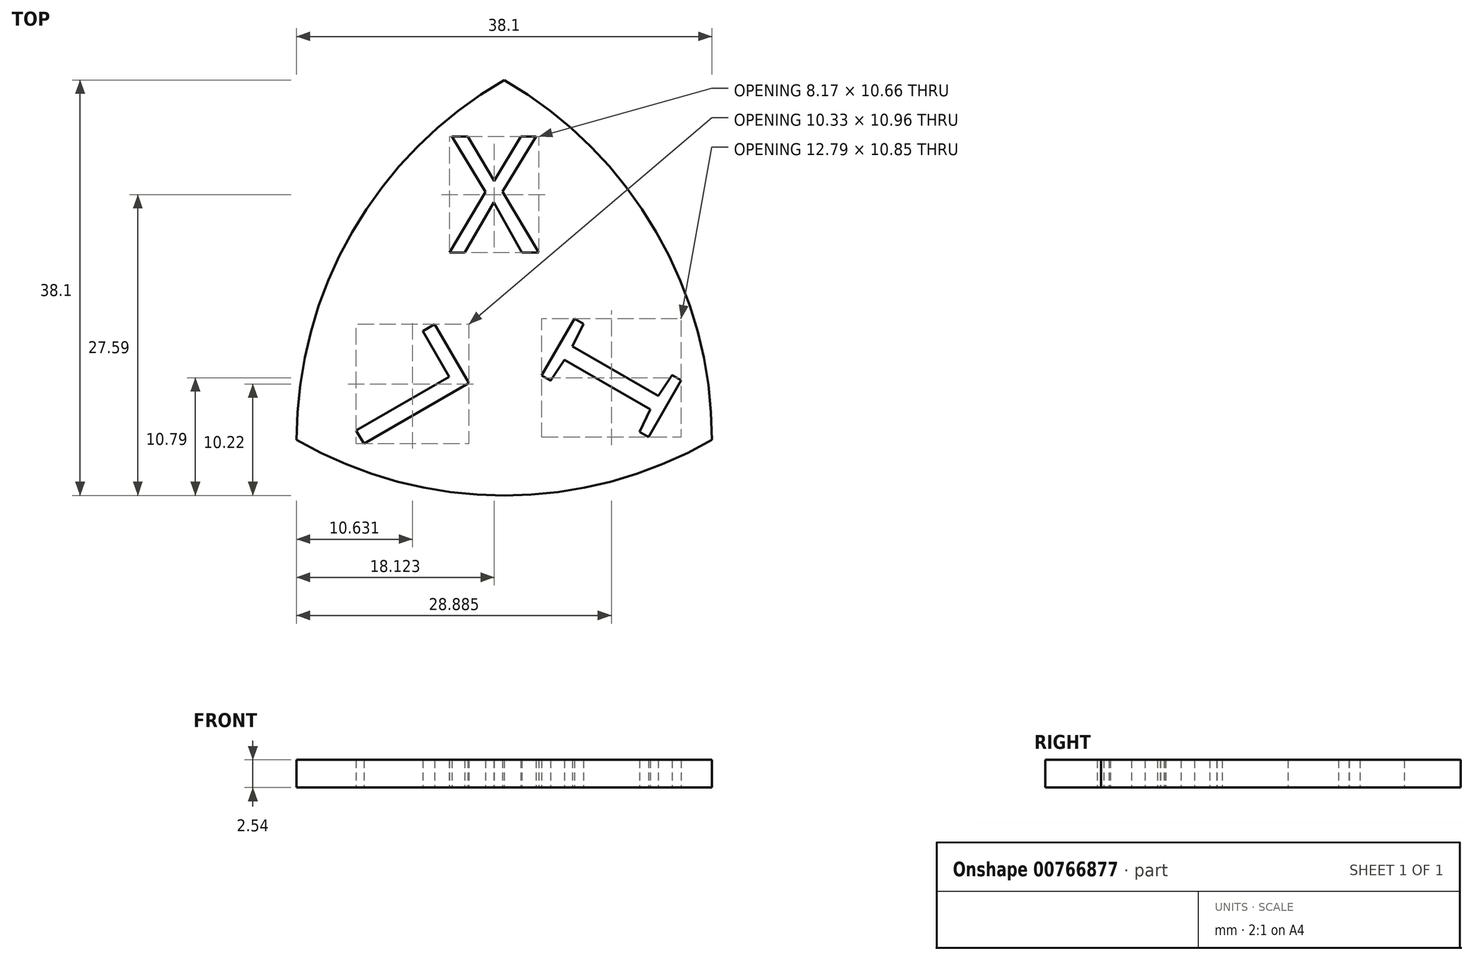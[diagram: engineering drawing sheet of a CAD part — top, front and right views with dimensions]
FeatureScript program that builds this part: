
annotation { "Feature Type Name" : "Feature", "Feature Type Description" : "" }
export const myFeature = defineFeature(function(context is Context, id is Id, definition is map)
    precondition{}
    {
        {
            var Q0;
            Q0=qCreatedBy(makeId("Top.planeOp"),FACE);
            var sketch = newSketch(context, id + "F0", { "sketchPlane" : qUnion([Q0])});
            skCircle(sketch, "E0", {"center": v(0, 0) * mm, "radius": 38.1 * mm});
            skSolve(sketch);
        }
        {
            var Q0;
            Q0=qCreatedBy(makeId("Top.planeOp"),FACE);
            var sketch = newSketch(context, id + "F1", { "sketchPlane" : qUnion([Q0])});
            skCircle(sketch, "E1", {"center": v(-38.1, 0) * mm, "radius": 38.1 * mm});
            skSolve(sketch);
        }
        {
            var Q0;
            Q0=qCreatedBy(makeId("Top.planeOp"),FACE);
            var sketch = newSketch(context, id + "F2", { "sketchPlane" : qUnion([Q0])});
            skCircle(sketch, "E2", {"center": v(-19.05, 33) * mm, "radius": 38.1 * mm});
            skSolve(sketch);
        }
        {
            var Q0;
            Q0=makeQuery(id+"F0.imprint","IMPRINT",FACE,{"disambiguationData":[TD([[makeQuery(id+"F0.imprint","IMPRINT",EDGE,{"derivedFrom":sQuery(id+"F0.wireOp",EDGE,"E0")}),1.0]])]});
            extrude(context, id + "F3", {"entities" : qUnion([Q0]), "depth" : 2.54 * mm, "offsetDistance" : 25.4 * mm});
        }
        {
            var Q0;
            Q0=makeQuery(id+"F2.imprint","IMPRINT",FACE,{"disambiguationData":[TD([[makeQuery(id+"F2.imprint","IMPRINT",EDGE,{"derivedFrom":sQuery(id+"F2.wireOp",EDGE,"E2")}),1.0]])]});
            extrude(context, id + "F4", {"entities" : qUnion([Q0]), "depth" : 2.54 * mm, "offsetDistance" : 25.4 * mm});
        }
        {
            var Q0;
            Q0=makeQuery(id+"F1.imprint","IMPRINT",FACE,{"disambiguationData":[TD([[makeQuery(id+"F1.imprint","IMPRINT",EDGE,{"derivedFrom":sQuery(id+"F1.wireOp",EDGE,"E1")}),1.0]])]});
            extrude(context, id + "F5", {"entities" : qUnion([Q0]), "depth" : 2.54 * mm, "offsetDistance" : 25.4 * mm});
        }
        {
            var Q0;
            Q0=makeQuery(id+"F4.opExtrude","SWEPT_BODY",BODY,{"disambiguationData":[OSD([sQuery(id+"F2.wireOp",EDGE,"E2")])]});
            var Q1;
            Q1=makeQuery(id+"F3.opExtrude","SWEPT_BODY",BODY,{"disambiguationData":[OSD([sQuery(id+"F0.wireOp",EDGE,"E0")])]});
            var Q2;
            Q2=makeQuery(id+"F5.opExtrude","SWEPT_BODY",BODY,{"disambiguationData":[OSD([sQuery(id+"F1.wireOp",EDGE,"E1")])]});
            booleanBodies(context, id + "F6", {"operationType" : BooleanOperationType.INTERSECTION, "tools" : qUnion([Q0, Q1, Q2])});
        }
        {
            var Q0;
            Q0=qCreatedBy(makeId("Top.planeOp"),FACE);
            var sketch = newSketch(context, id + "F7", { "sketchPlane" : qUnion([Q0])});
            skText(sketch, "E3", { "text": "X", "fontName": "DroidSansMono.ttf"});
            skText(sketch, "E4", { "text": "L", "fontName": "DroidSansMono.ttf"});
            skText(sketch, "E5", { "text": "I", "fontName": "DroidSansMono.ttf"});
            const initialGuessF7  = {"E3": [-0.02445, 0.01716, 1, 0, 0.01075], "E4": [-0.02142, 0.00366, -0.5, 0.86603, 0.0112], "E5": [-0.01174, 0.01262, -0.5, -0.86603, 0.0114]};
            skSetInitialGuess(sketch, initialGuessF7);
            skSolve(sketch);
        }
        {
            var Q0;
            Q0 = qSketchRegion(id + "F7", true);
            extrude(context, id + "F8", {"entities" : qUnion([Q0]), "depth" : 2.54 * mm, "offsetDistance" : 25.4 * mm});
        }
        {
            var Q0;
            Q0=makeQuery(id+"F8.opExtrude","SWEPT_BODY",BODY,{"disambiguationData":[OSD([sQuery(id+"F7.wireOp",EDGE,"E3.sketch_text.stroke-0"),sQuery(id+"F7.wireOp",EDGE,"E3.sketch_text.stroke-1"),sQuery(id+"F7.wireOp",EDGE,"E3.sketch_text.stroke-2"),sQuery(id+"F7.wireOp",EDGE,"E3.sketch_text.stroke-3"),sQuery(id+"F7.wireOp",EDGE,"E3.sketch_text.stroke-4"),sQuery(id+"F7.wireOp",EDGE,"E3.sketch_text.stroke-5"),sQuery(id+"F7.wireOp",EDGE,"E3.sketch_text.stroke-6"),sQuery(id+"F7.wireOp",EDGE,"E3.sketch_text.stroke-7"),sQuery(id+"F7.wireOp",EDGE,"E3.sketch_text.stroke-8"),sQuery(id+"F7.wireOp",EDGE,"E3.sketch_text.stroke-9"),sQuery(id+"F7.wireOp",EDGE,"E3.sketch_text.stroke-10"),sQuery(id+"F7.wireOp",EDGE,"E3.sketch_text.stroke-11")])]});
            var Q1;
            Q1=makeQuery(id+"F8.opExtrude","SWEPT_BODY",BODY,{"disambiguationData":[OSD([sQuery(id+"F7.wireOp",EDGE,"E4.sketch_text.stroke-0"),sQuery(id+"F7.wireOp",EDGE,"E4.sketch_text.stroke-1"),sQuery(id+"F7.wireOp",EDGE,"E4.sketch_text.stroke-2"),sQuery(id+"F7.wireOp",EDGE,"E4.sketch_text.stroke-3"),sQuery(id+"F7.wireOp",EDGE,"E4.sketch_text.stroke-4"),sQuery(id+"F7.wireOp",EDGE,"E4.sketch_text.stroke-5")])]});
            var Q2;
            Q2=makeQuery(id+"F8.opExtrude","SWEPT_BODY",BODY,{"disambiguationData":[OSD([sQuery(id+"F7.wireOp",EDGE,"E5.sketch_text.stroke-0"),sQuery(id+"F7.wireOp",EDGE,"E5.sketch_text.stroke-1"),sQuery(id+"F7.wireOp",EDGE,"E5.sketch_text.stroke-2"),sQuery(id+"F7.wireOp",EDGE,"E5.sketch_text.stroke-3"),sQuery(id+"F7.wireOp",EDGE,"E5.sketch_text.stroke-4"),sQuery(id+"F7.wireOp",EDGE,"E5.sketch_text.stroke-5"),sQuery(id+"F7.wireOp",EDGE,"E5.sketch_text.stroke-6"),sQuery(id+"F7.wireOp",EDGE,"E5.sketch_text.stroke-7"),sQuery(id+"F7.wireOp",EDGE,"E5.sketch_text.stroke-8"),sQuery(id+"F7.wireOp",EDGE,"E5.sketch_text.stroke-9"),sQuery(id+"F7.wireOp",EDGE,"E5.sketch_text.stroke-10"),sQuery(id+"F7.wireOp",EDGE,"E5.sketch_text.stroke-11")])]});
            var Q3;
            Q3=makeQuery(id+"F6.opBoolean","INTERSECT",BODY,{"derivedFrom":[makeQuery(id+"F3.opExtrude","SWEPT_BODY",BODY,{"disambiguationData":[OSD([sQuery(id+"F0.wireOp",EDGE,"E0")])]}),makeQuery(id+"F4.opExtrude","SWEPT_BODY",BODY,{"disambiguationData":[OSD([sQuery(id+"F2.wireOp",EDGE,"E2")])]}),makeQuery(id+"F5.opExtrude","SWEPT_BODY",BODY,{"disambiguationData":[OSD([sQuery(id+"F1.wireOp",EDGE,"E1")])]})]});
            booleanBodies(context, id + "F9", {"operationType" : BooleanOperationType.SUBTRACTION, "tools" : qUnion([Q0, Q1, Q2]), "targets" : qUnion([Q3])});
        }
    });
